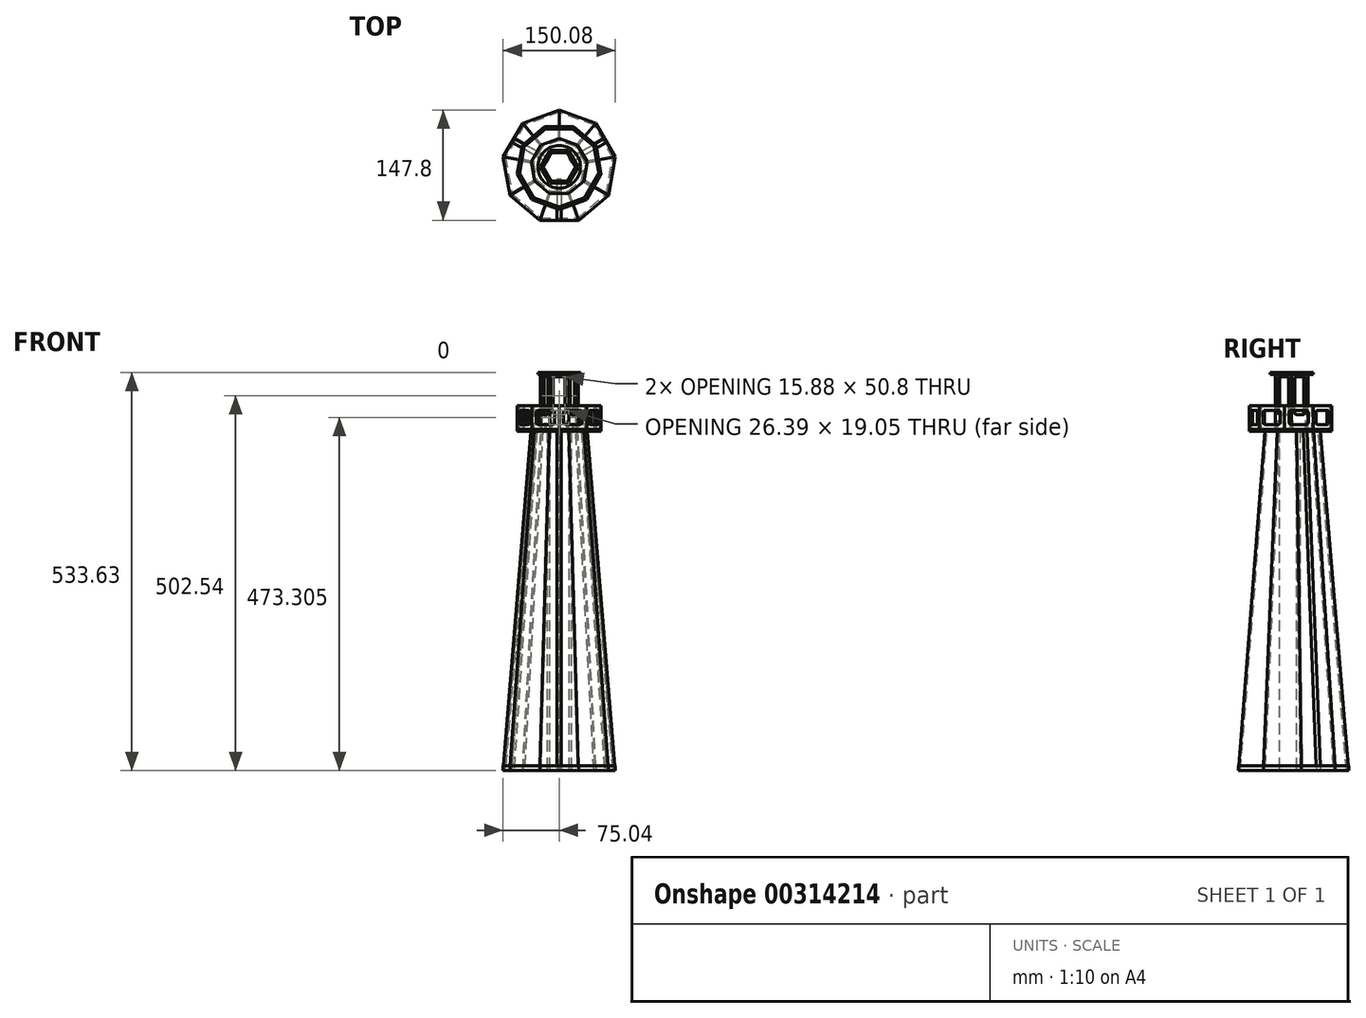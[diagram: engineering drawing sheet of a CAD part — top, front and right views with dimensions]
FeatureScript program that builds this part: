
annotation { "Feature Type Name" : "Feature", "Feature Type Description" : "" }
export const myFeature = defineFeature(function(context is Context, id is Id, definition is map)
    precondition{}
    {
        {
            var Q0;
            Q0=qCreatedBy(makeId("Front.planeOp"),FACE);
            var sketch = newSketch(context, id + "F0", { "sketchPlane" : qUnion([Q0])});
            skLineSegment(sketch, "E0", {"start": v(0, 0) * mm, "end": v(0, 609.6) * mm, "construction": true});
            skSolve(sketch);
        }
        {
            var Q0;
            Q0=qCreatedBy(makeId("Top.planeOp"),FACE);
            var sketch = newSketch(context, id + "F1", { "sketchPlane" : qUnion([Q0])});
            skCircle(sketch, "E1.cCircle", {"center": v(0, 0) * mm, "radius": 76.2 * mm, "construction": true});
            skLineSegment(sketch, "E1.0", {"start": v(0, 76.2) * mm, "end": v(48.98, 58.37) * mm});
            skLineSegment(sketch, "E1.1", {"start": v(48.98, 58.37) * mm, "end": v(75.04, 13.23) * mm});
            skLineSegment(sketch, "E1.2", {"start": v(75.04, 13.23) * mm, "end": v(66, -38.1) * mm});
            skLineSegment(sketch, "E1.3", {"start": v(66, -38.1) * mm, "end": v(26.06, -71.6) * mm});
            skLineSegment(sketch, "E1.4", {"start": v(26.06, -71.6) * mm, "end": v(-26.06, -71.6) * mm});
            skLineSegment(sketch, "E1.5", {"start": v(-26.06, -71.6) * mm, "end": v(-66, -38.1) * mm});
            skLineSegment(sketch, "E1.6", {"start": v(-66, -38.1) * mm, "end": v(-75.04, 13.23) * mm});
            skLineSegment(sketch, "E1.7", {"start": v(-75.04, 13.23) * mm, "end": v(-48.98, 58.37) * mm});
            skLineSegment(sketch, "E1.8", {"start": v(-48.98, 58.37) * mm, "end": v(0, 76.2) * mm});
            skSolve(sketch);
        }
        {
            var Q0;
            Q0=qCreatedBy(makeId("Top.planeOp"),FACE);
            cPlane(context, id + "F2", {"entities" : qUnion([Q0]), "cplaneType" : CPlaneType.OFFSET, "offset" : 457.2 * mm, "width" : 152.4 * mm, "height" : 152.4 * mm});
        }
        {
            var Q0;
            Q0=qCreatedBy(id+"F2.planeOp",FACE);
            var sketch = newSketch(context, id + "F3", { "sketchPlane" : qUnion([Q0])});
            skCircle(sketch, "E2.cCircle", {"center": v(0, 0) * mm, "radius": 38.1 * mm, "construction": true});
            skLineSegment(sketch, "E2.0", {"start": v(0, 38.1) * mm, "end": v(24.5, 29.19) * mm});
            skLineSegment(sketch, "E2.1", {"start": v(24.5, 29.19) * mm, "end": v(37.52, 6.62) * mm});
            skLineSegment(sketch, "E2.2", {"start": v(37.52, 6.62) * mm, "end": v(33, -19.05) * mm});
            skLineSegment(sketch, "E2.3", {"start": v(33, -19.05) * mm, "end": v(13.03, -35.8) * mm});
            skLineSegment(sketch, "E2.4", {"start": v(13.03, -35.8) * mm, "end": v(-13.03, -35.8) * mm});
            skLineSegment(sketch, "E2.5", {"start": v(-13.03, -35.8) * mm, "end": v(-33, -19.05) * mm});
            skLineSegment(sketch, "E2.6", {"start": v(-33, -19.05) * mm, "end": v(-37.52, 6.62) * mm});
            skLineSegment(sketch, "E2.7", {"start": v(-37.52, 6.62) * mm, "end": v(-24.5, 29.19) * mm});
            skLineSegment(sketch, "E2.8", {"start": v(-24.5, 29.19) * mm, "end": v(0, 38.1) * mm});
            skCircle(sketch, "E3.cCircle", {"center": v(0, 0) * mm, "radius": 57.15 * mm, "construction": true});
            skLineSegment(sketch, "E3.0", {"start": v(0, -57.15) * mm, "end": v(-36.74, -43.78) * mm});
            skLineSegment(sketch, "E3.1", {"start": v(-36.74, -43.78) * mm, "end": v(-56.28, -9.92) * mm});
            skLineSegment(sketch, "E3.2", {"start": v(-56.28, -9.92) * mm, "end": v(-49.5, 28.58) * mm});
            skLineSegment(sketch, "E3.3", {"start": v(-49.5, 28.57) * mm, "end": v(-19.55, 53.7) * mm});
            skLineSegment(sketch, "E3.4", {"start": v(-19.55, 53.7) * mm, "end": v(19.55, 53.7) * mm});
            skLineSegment(sketch, "E3.5", {"start": v(19.55, 53.7) * mm, "end": v(49.5, 28.58) * mm});
            skLineSegment(sketch, "E3.6", {"start": v(49.5, 28.58) * mm, "end": v(56.28, -9.92) * mm});
            skLineSegment(sketch, "E3.7", {"start": v(56.28, -9.92) * mm, "end": v(36.74, -43.78) * mm});
            skLineSegment(sketch, "E3.8", {"start": v(36.74, -43.78) * mm, "end": v(0, -57.15) * mm});
            skCircle(sketch, "E4.cCircle", {"center": v(0, 0) * mm, "radius": 25.4 * mm, "construction": true});
            skLineSegment(sketch, "E4.0", {"start": v(25.4, 0) * mm, "end": v(12.7, -22) * mm});
            skLineSegment(sketch, "E4.1", {"start": v(12.7, -22) * mm, "end": v(-12.7, -22) * mm});
            skLineSegment(sketch, "E4.2", {"start": v(-12.7, -22) * mm, "end": v(-25.4, 0) * mm});
            skLineSegment(sketch, "E4.3", {"start": v(-25.4, 0) * mm, "end": v(-12.7, 22) * mm});
            skLineSegment(sketch, "E4.4", {"start": v(-12.7, 22) * mm, "end": v(12.7, 22) * mm});
            skLineSegment(sketch, "E4.5", {"start": v(12.7, 22) * mm, "end": v(25.4, 0) * mm});
            skSolve(sketch);
        }
        {
            var Q0;
            Q0=sQuery(id+"F1.wireOp",VERTEX,"E1.5.start");
            var Q1;
            Q1=sQuery(id+"F1.wireOp",VERTEX,"E1.4.start");
            var Q2;
            Q2=sQuery(id+"F3.wireOp",VERTEX,"E2.5.start");
            cPlane(context, id + "F4", {"entities" : qUnion([Q0, Q1, Q2]), "cplaneType" : CPlaneType.THREE_POINT, "offset" : 25.4 * mm, "width" : 152.4 * mm, "height" : 152.4 * mm});
        }
        {
            var Q0;
            Q0=qCreatedBy(id+"F4.planeOp",FACE);
            var sketch = newSketch(context, id + "F5", { "sketchPlane" : qUnion([Q0])});
            skPoint(sketch, "E5.0", {"position": v(13.03, 453) * mm});
            skPoint(sketch, "E6.0", {"position": v(-13.03, 453) * mm});
            skPoint(sketch, "E7.0", {"position": v(-26.06, -5.6) * mm});
            skPoint(sketch, "E8.0", {"position": v(26.06, -5.6) * mm});
            skLineSegment(sketch, "E9", {"start": v(-26.06, -5.6) * mm, "end": v(-13.03, 453) * mm});
            skLineSegment(sketch, "E10", {"start": v(13.03, 453) * mm, "end": v(-13.03, 453) * mm});
            skLineSegment(sketch, "E11", {"start": v(13.03, 453) * mm, "end": v(26.06, -5.6) * mm});
            skLineSegment(sketch, "E12", {"start": v(26.06, -5.6) * mm, "end": v(-26.06, -5.6) * mm});
            skSolve(sketch);
        }
        {
            var Q0;
            Q0=qCreatedBy(makeId("Right.planeOp"),FACE);
            var sketch = newSketch(context, id + "F6", { "sketchPlane" : qUnion([Q0])});
            skLineSegment(sketch, "E13.0", {"start": v(-35.8, 457.2) * mm, "end": v(-71.6, 0) * mm});
            skLineSegment(sketch, "E14", {"start": v(-35.8, 457.2) * mm, "end": v(-16.75, 457.2) * mm});
            skLineSegment(sketch, "E15", {"start": v(-16.75, 457.2) * mm, "end": v(-16.75, 0) * mm});
            skLineSegment(sketch, "E16", {"start": v(-16.75, 0) * mm, "end": v(-71.6, 0) * mm});
            skLineSegment(sketch, "E17.0", {"start": v(-36.04, 454.2) * mm, "end": v(-16.75, 454.2) * mm});
            skSolve(sketch);
        }
        {
            var Q0;
            Q0=qCreatedBy(makeId("Front.planeOp"),FACE);
            var Q1;
            Q1=sQuery(id+"F3.wireOp",VERTEX,"E3.4.start");
            cPlane(context, id + "F7", {"entities" : qUnion([Q0, Q1]), "cplaneType" : CPlaneType.PLANE_POINT, "offset" : 25.4 * mm, "width" : 152.4 * mm, "height" : 152.4 * mm});
        }
        {
            var Q0;
            Q0=qCreatedBy(id+"F7.planeOp",FACE);
            var sketch = newSketch(context, id + "F8", { "sketchPlane" : qUnion([Q0])});
            skPoint(sketch, "E18.0", {"position": v(19.55, 457.2) * mm});
            skPoint(sketch, "E19.0", {"position": v(-19.55, 457.2) * mm});
            skLineSegment(sketch, "E20.bottom", {"start": v(19.55, 457.2) * mm, "end": v(-19.55, 457.2) * mm});
            skLineSegment(sketch, "E20.top", {"start": v(19.55, 488.95) * mm, "end": v(-19.55, 488.95) * mm});
            skLineSegment(sketch, "E20.left", {"start": v(19.55, 457.2) * mm, "end": v(19.55, 488.95) * mm});
            skLineSegment(sketch, "E20.right", {"start": v(-19.55, 457.2) * mm, "end": v(-19.55, 488.95) * mm});
            skLineSegment(sketch, "E21.0", {"start": v(10.02, 482.6) * mm, "end": v(-10.02, 482.6) * mm});
            skLineSegment(sketch, "E21.1", {"start": v(13.2, 466.73) * mm, "end": v(13.2, 479.43) * mm});
            skLineSegment(sketch, "E21.2", {"start": v(10.02, 463.55) * mm, "end": v(-10.02, 463.55) * mm});
            skLineSegment(sketch, "E21.3", {"start": v(-13.2, 466.73) * mm, "end": v(-13.2, 479.43) * mm});
            skPoint(sketch, "E22.visualSharp", {"position": v(13.2, 482.6) * mm});
            skArc(sketch, "E22.filletArc", {"start": v(13.2, 479.43) * mm, "mid": v(12.27, 481.67) * mm, "end": v(10.02, 482.6) * mm});
            skPoint(sketch, "E23.visualSharp", {"position": v(13.2, 463.55) * mm});
            skArc(sketch, "E23.filletArc", {"start": v(10.02, 463.55) * mm, "mid": v(12.27, 464.48) * mm, "end": v(13.2, 466.73) * mm});
            skPoint(sketch, "E24.visualSharp", {"position": v(-13.2, 463.55) * mm});
            skArc(sketch, "E24.filletArc", {"start": v(-13.2, 466.73) * mm, "mid": v(-12.27, 464.48) * mm, "end": v(-10.02, 463.55) * mm});
            skPoint(sketch, "E25.visualSharp", {"position": v(-13.2, 482.6) * mm});
            skArc(sketch, "E25.filletArc", {"start": v(-10.02, 482.6) * mm, "mid": v(-12.27, 481.67) * mm, "end": v(-13.2, 479.43) * mm});
            skLineSegment(sketch, "E26.top", {"start": v(19.55, 454.2) * mm, "end": v(-19.55, 454.2) * mm});
            skLineSegment(sketch, "E26.left", {"start": v(19.55, 457.2) * mm, "end": v(19.55, 454.2) * mm});
            skLineSegment(sketch, "E26.right", {"start": v(-19.55, 457.2) * mm, "end": v(-19.55, 454.2) * mm});
            skSolve(sketch);
        }
        {
            var Q0;
            Q0=qCreatedBy(makeId("Front.planeOp"),FACE);
            var Q1;
            Q1=sQuery(id+"F3.wireOp",VERTEX,"E4.1.end");
            cPlane(context, id + "F9", {"entities" : qUnion([Q0, Q1]), "cplaneType" : CPlaneType.PLANE_POINT, "offset" : 25.4 * mm, "width" : 152.4 * mm, "height" : 152.4 * mm});
        }
        {
            var Q0;
            Q0=qCreatedBy(id+"F9.planeOp",FACE);
            var sketch = newSketch(context, id + "F10", { "sketchPlane" : qUnion([Q0])});
            skPoint(sketch, "E27.0", {"position": v(-12.7, 457.2) * mm});
            skPoint(sketch, "E28.0", {"position": v(12.7, 457.2) * mm});
            skLineSegment(sketch, "E29.bottom", {"start": v(-12.7, 454.2) * mm, "end": v(12.7, 454.2) * mm});
            skLineSegment(sketch, "E29.top", {"start": v(-12.7, 533.4) * mm, "end": v(12.7, 533.4) * mm});
            skLineSegment(sketch, "E29.left", {"start": v(-12.7, 454.2) * mm, "end": v(-12.7, 533.4) * mm});
            skLineSegment(sketch, "E29.right", {"start": v(12.7, 454.2) * mm, "end": v(12.7, 533.4) * mm});
            skLineSegment(sketch, "E30.bottom", {"start": v(-4.76, 476.91) * mm, "end": v(4.76, 476.91) * mm});
            skLineSegment(sketch, "E30.top", {"start": v(-4.76, 527.71) * mm, "end": v(4.76, 527.71) * mm});
            skLineSegment(sketch, "E30.left", {"start": v(-7.94, 480.09) * mm, "end": v(-7.94, 524.54) * mm});
            skLineSegment(sketch, "E30.right", {"start": v(7.94, 480.09) * mm, "end": v(7.94, 524.54) * mm});
            skPoint(sketch, "E31.visualSharp", {"position": v(-7.94, 527.71) * mm});
            skArc(sketch, "E31.filletArc", {"start": v(-4.76, 527.71) * mm, "mid": v(-7, 526.78) * mm, "end": v(-7.94, 524.54) * mm});
            skPoint(sketch, "E32.visualSharp", {"position": v(7.94, 527.71) * mm});
            skArc(sketch, "E32.filletArc", {"start": v(7.94, 524.54) * mm, "mid": v(7, 526.78) * mm, "end": v(4.76, 527.71) * mm});
            skPoint(sketch, "E33.visualSharp", {"position": v(7.94, 476.91) * mm});
            skArc(sketch, "E33.filletArc", {"start": v(4.76, 476.91) * mm, "mid": v(7, 477.84) * mm, "end": v(7.94, 480.09) * mm});
            skPoint(sketch, "E34.visualSharp", {"position": v(-7.94, 476.91) * mm});
            skArc(sketch, "E34.filletArc", {"start": v(-7.94, 480.09) * mm, "mid": v(-7, 477.84) * mm, "end": v(-4.76, 476.91) * mm});
            skSolve(sketch);
        }
        {
            var Q0;
            Q0=qCreatedBy(makeId("Top.planeOp"),FACE);
            var Q1;
            Q1=sQuery(id+"F10.wireOp",VERTEX,"E29.left.end");
            cPlane(context, id + "F11", {"entities" : qUnion([Q0, Q1]), "cplaneType" : CPlaneType.PLANE_POINT, "offset" : 25.4 * mm, "width" : 152.4 * mm, "height" : 152.4 * mm});
        }
        {
            var Q0;
            Q0=qCreatedBy(id+"F11.planeOp",FACE);
            var sketch = newSketch(context, id + "F12", { "sketchPlane" : qUnion([Q0])});
            skCircle(sketch, "E35", {"center": v(0, 0) * mm, "radius": 28.58 * mm});
            skSolve(sketch);
        }
        {
            var Q0;
            Q0=qSketchRegion(id+"F1",true);
            extrude(context, id + "F13", {"entities" : qUnion([Q0]), "depth" : 6 * mm});
        }
        {
            var Q0;
            Q0=qSketchRegion(id+"F5",true);
            extrude(context, id + "F14", {"entities" : qUnion([Q0]), "depth" : 3 * mm});
        }
        {
            var Q0;
            {var subQ0=sQuery(id+"F6.wireOp",EDGE,"E16");Q0=makeQuery(id+"F6.imprint","IMPRINT",FACE,{"disambiguationData":[TD([[makeQuery(id+"F6.imprint","IMPRINT",EDGE,{"derivedFrom":subQ0}),-1.0]])]});}
            extrude(context, id + "F15", {"entities" : qUnion([Q0]), "depth" : 6 * mm, "symmetric" : true});
        }
        {
            var Q0;
            Q0=qSketchRegion(id+"F3",true);
            var Q1;
            Q1=makeQuery(id+"F3.imprint","IMPRINT",FACE,{"disambiguationData":[TD([[makeQuery(id+"F3.imprint","IMPRINT",EDGE,{"derivedFrom":sQuery(id+"F3.wireOp",EDGE,"E2.0")}),-1.0]])]});
            var Q2;
            Q2=makeQuery(id+"F3.imprint","IMPRINT",FACE,{"disambiguationData":[TD([[makeQuery(id+"F3.imprint","IMPRINT",EDGE,{"derivedFrom":sQuery(id+"F3.wireOp",EDGE,"E4.0")}),-1.0]])]});
            extrude(context, id + "F16", {"entities" : qUnion([Q0, Q1, Q2]), "oppositeDirection" : true, "depth" : 3 * mm});
        }
        {
            var Q0;
            Q0=qSketchRegion(id+"F8",true);
            extrude(context, id + "F17", {"entities" : qUnion([Q0]), "depth" : 3 * mm});
        }
        {
            var Q0;
            Q0=qSketchRegion(id+"F10",true);
            extrude(context, id + "F18", {"entities" : qUnion([Q0]), "oppositeDirection" : true, "depth" : 3 * mm});
        }
        {
            var Q0;
            Q0=makeQuery(id+"F12.imprint","IMPRINT",FACE,{"disambiguationData":[TD([[makeQuery(id+"F12.imprint","IMPRINT",EDGE,{"derivedFrom":sQuery(id+"F12.wireOp",EDGE,"E35")}),1.0]])]});
            extrude(context, id + "F19", {"entities" : qUnion([Q0]), "oppositeDirection" : true, "depth" : 3 * mm});
        }
        {
            var Q0;
            Q0=makeQuery(id+"F15.opExtrude","SWEPT_BODY",BODY,{"disambiguationData":[OSD([sQuery(id+"F6.wireOp",EDGE,"E13.0"),sQuery(id+"F6.wireOp",EDGE,"E15"),sQuery(id+"F6.wireOp",EDGE,"E16"),sQuery(id+"F6.wireOp",EDGE,"E17.0")])]});
            var Q1;
            Q1=sQuery(id+"F0.wireOp",EDGE,"E0");
            circularPattern(context, id + "F20", {"entities" : qUnion([Q0]), "axis" : qUnion([Q1]), "angle" : 360 * degree, "instanceCount" : 3, "equalSpace" : true});
        }
        {
            var Q0;
            Q0=makeQuery(id+"F17.opExtrude","SWEPT_BODY",BODY,{"disambiguationData":[OSD([sQuery(id+"F8.wireOp",EDGE,"E20.top"),sQuery(id+"F8.wireOp",EDGE,"E20.left"),sQuery(id+"F8.wireOp",EDGE,"E20.right"),sQuery(id+"F8.wireOp",EDGE,"E21.0"),sQuery(id+"F8.wireOp",EDGE,"E21.1"),sQuery(id+"F8.wireOp",EDGE,"E21.2"),sQuery(id+"F8.wireOp",EDGE,"E21.3"),sQuery(id+"F8.wireOp",EDGE,"E22.filletArc"),sQuery(id+"F8.wireOp",EDGE,"E23.filletArc"),sQuery(id+"F8.wireOp",EDGE,"E24.filletArc"),sQuery(id+"F8.wireOp",EDGE,"E25.filletArc"),sQuery(id+"F8.wireOp",EDGE,"E26.top"),sQuery(id+"F8.wireOp",EDGE,"E26.left"),sQuery(id+"F8.wireOp",EDGE,"E26.right")])]});
            var Q1;
            Q1=makeQuery(id+"F14.opExtrude","SWEPT_BODY",BODY,{"disambiguationData":[OSD([sQuery(id+"F5.wireOp",EDGE,"E9"),sQuery(id+"F5.wireOp",EDGE,"E10"),sQuery(id+"F5.wireOp",EDGE,"E11"),sQuery(id+"F5.wireOp",EDGE,"E12")])]});
            var Q2;
            Q2=sQuery(id+"F0.wireOp",EDGE,"E0");
            circularPattern(context, id + "F21", {"entities" : qUnion([Q0, Q1]), "axis" : qUnion([Q2]), "angle" : 360 * degree, "instanceCount" : 9, "equalSpace" : true});
        }
        {
            var Q0;
            Q0=makeQuery(id+"F18.opExtrude","SWEPT_BODY",BODY,{"disambiguationData":[OSD([sQuery(id+"F10.wireOp",EDGE,"E29.bottom"),sQuery(id+"F10.wireOp",EDGE,"E29.top"),sQuery(id+"F10.wireOp",EDGE,"E29.left"),sQuery(id+"F10.wireOp",EDGE,"E29.right"),sQuery(id+"F10.wireOp",EDGE,"E30.bottom"),sQuery(id+"F10.wireOp",EDGE,"E30.top"),sQuery(id+"F10.wireOp",EDGE,"E30.left"),sQuery(id+"F10.wireOp",EDGE,"E30.right"),sQuery(id+"F10.wireOp",EDGE,"E31.filletArc"),sQuery(id+"F10.wireOp",EDGE,"E32.filletArc"),sQuery(id+"F10.wireOp",EDGE,"E33.filletArc"),sQuery(id+"F10.wireOp",EDGE,"E34.filletArc")])]});
            var Q1;
            Q1=makeQuery(id+"FZdNMvIbFvd73A2_6.opExtrude","SWEPT_BODY",BODY,{"disambiguationData":[OSD([sQuery(id+"F12.wireOp",EDGE,"PxiaAuuB-iNYM-JTBi-DcXQ-ODUsAWQNwEHI"),sQuery(id+"F12.wireOp",EDGE,"QswuuGaN-9mBv-JwoU-aKyc-UiZnDVxR1k9x"),sQuery(id+"F12.wireOp",EDGE,"YqK2sufa-QmS7-8hII-80hB-3HZfqvGuOiba")])]});
            var Q2;
            Q2=sQuery(id+"F0.wireOp",EDGE,"E0");
            circularPattern(context, id + "F22", {"entities" : qUnion([Q0, Q1]), "axis" : qUnion([Q2]), "angle" : 360 * degree, "instanceCount" : 6, "equalSpace" : true});
        }
    });
